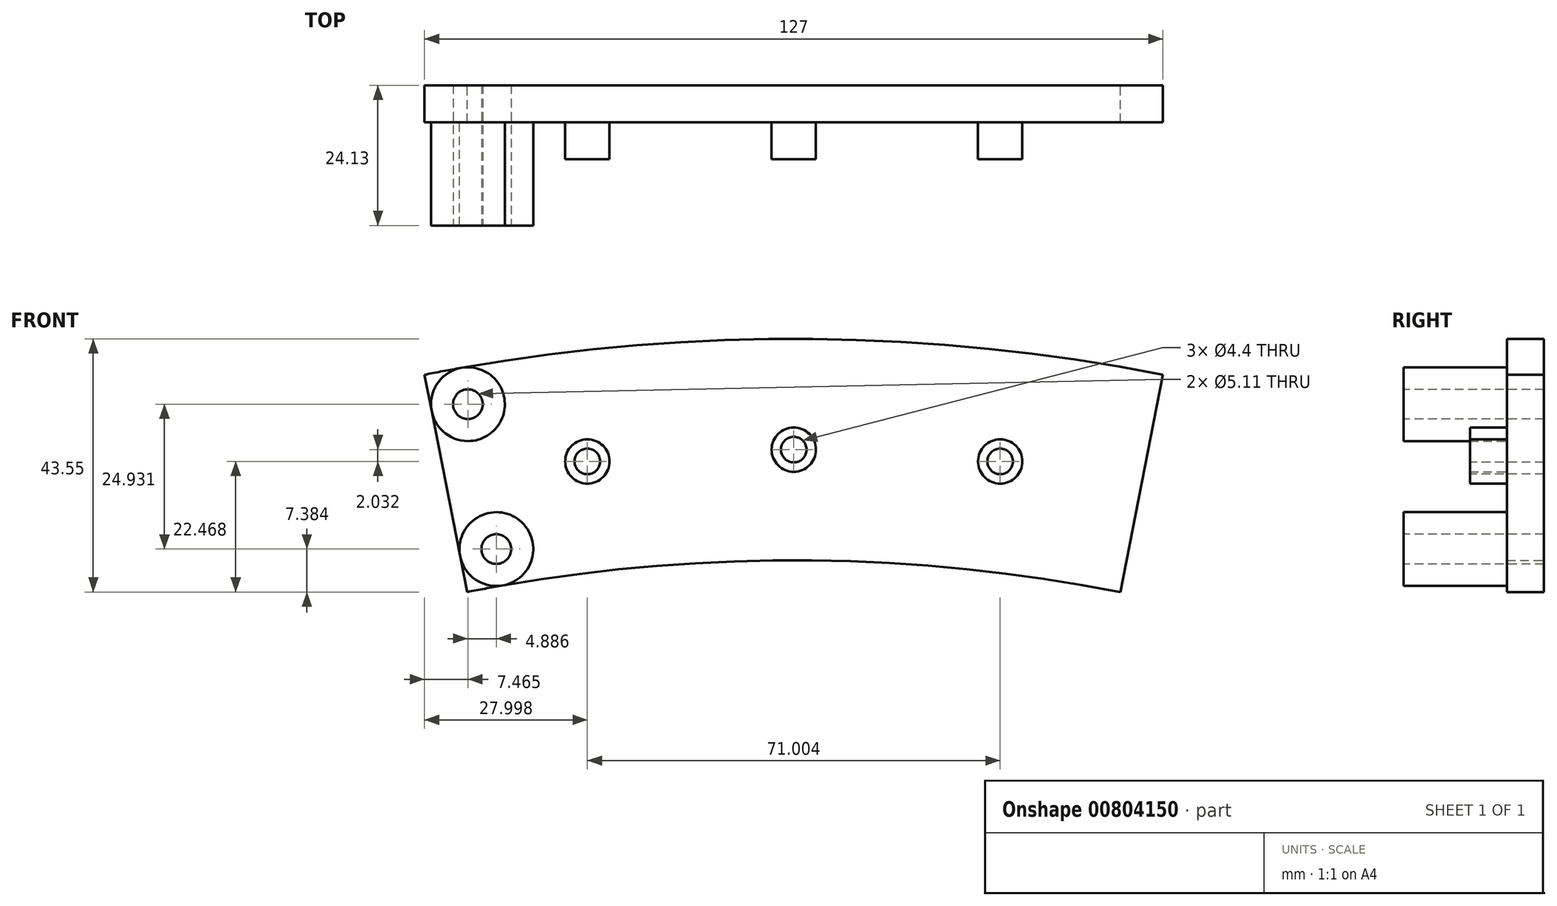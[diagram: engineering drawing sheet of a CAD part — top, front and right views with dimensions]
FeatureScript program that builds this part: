
annotation { "Feature Type Name" : "Feature", "Feature Type Description" : "" }
export const myFeature = defineFeature(function(context is Context, id is Id, definition is map)
    precondition{}
    {
        {
            var Q0;
            Q0=qCreatedBy(makeId("Front.planeOp"),FACE);
            var sketch = newSketch(context, id + "F0", { "sketchPlane" : qUnion([Q0])});
            skArc(sketch, "E0", {"start": v(63.5, 324.04) * mm, "mid": v(0, 330.2) * mm, "end": v(-63.5, 324.04) * mm});
            skLineSegment(sketch, "E1", {"start": v(-56.17, 286.65) * mm, "end": v(-63.5, 324.04) * mm});
            skLineSegment(sketch, "E2", {"start": v(56.17, 286.65) * mm, "end": v(63.5, 324.04) * mm});
            skLineSegment(sketch, "E3", {"start": v(-63.5, 324.04) * mm, "end": v(63.5, 324.04) * mm, "construction": true});
            skArc(sketch, "E4.0", {"start": v(56.17, 286.65) * mm, "mid": v(0, 292.1) * mm, "end": v(-56.17, 286.65) * mm});
            skSolve(sketch);
        }
        {
            var Q0;
            Q0 = qSketchRegion(id + "F0", true);
            extrude(context, id + "F1", {"entities" : qUnion([Q0]), "depth" : 6.35 * mm, "offsetDistance" : 25.4 * mm});
        }
        {
            var Q0;
            Q0=makeQuery(id+"F1.opExtrude","CAP_FACE",FACE,{"disambiguationData":[OSD([sQuery(id+"F0.wireOp",EDGE,"E0"),sQuery(id+"F0.wireOp",EDGE,"E1"),sQuery(id+"F0.wireOp",EDGE,"E2"),sQuery(id+"F0.wireOp",EDGE,"E4.0")])],"isStart":false});
            var sketch = newSketch(context, id + "F2", { "sketchPlane" : qUnion([Q0])});
            skPoint(sketch, "E5.1.end.orphan", {"position": v(-63.5, 324.04) * mm});
            skPoint(sketch, "E5.1.start.orphan", {"position": v(-56.17, 286.65) * mm});
            skLineSegment(sketch, "E6.0", {"start": v(-56.17, 286.65) * mm, "end": v(-63.5, 324.04) * mm, "construction": true});
            skLineSegment(sketch, "E7", {"start": v(-57.26, 325.2) * mm, "end": v(-49.93, 287.8) * mm, "construction": true});
            skArc(sketch, "E8.0", {"start": v(63.5, 324.04) * mm, "mid": v(0, 330.2) * mm, "end": v(-63.5, 324.04) * mm, "construction": true});
            skArc(sketch, "E9.0", {"start": v(56.17, 286.65) * mm, "mid": v(0, 292.1) * mm, "end": v(-56.17, 286.65) * mm, "construction": true});
            skCircle(sketch, "E10", {"center": v(-51.15, 294.03) * mm, "radius": 6.35 * mm});
            skCircle(sketch, "E11", {"center": v(-56.04, 318.97) * mm, "radius": 6.35 * mm});
            skSolve(sketch);
        }
        {
            var Q0;
            Q0 = qSketchRegion(id + "F2", true);
            extrude(context, id + "F3", {"entities" : qUnion([Q0]), "operationType" : NewBodyOperationType.ADD, "depth" : 17.78 * mm, "offsetDistance" : 25.4 * mm});
        }
        {
            var Q0;
            Q0=makeQuery(id+"F3.opExtrude","CAP_FACE",FACE,{"disambiguationData":[OSD([sQuery(id+"F2.wireOp",EDGE,"E11")])],"isStart":false});
            var sketch = newSketch(context, id + "F4", { "sketchPlane" : qUnion([Q0])});
            skCircle(sketch, "E12.0", {"center": v(-56.04, 318.97) * mm, "radius": 6.35 * mm, "construction": true});
            skCircle(sketch, "E12.1", {"center": v(-51.15, 294.03) * mm, "radius": 6.35 * mm, "construction": true});
            skSolve(sketch);
        }
        {
            var Q0;
            Q0=sQuery(id+"F4.wireOp",VERTEX,"E12.0.center");
            var Q1;
            Q1=sQuery(id+"F4.wireOp",VERTEX,"E12.1.center");
            var Q2;
            Q2=makeQuery(id+"F1.opExtrude","SWEPT_BODY",BODY,{"disambiguationData":[OSD([sQuery(id+"F0.wireOp",EDGE,"E0"),sQuery(id+"F0.wireOp",EDGE,"E1"),sQuery(id+"F0.wireOp",EDGE,"E2"),sQuery(id+"F0.wireOp",EDGE,"E4.0")])]});
            hole(context, id + "F5", {"style" : HoleStyle.SIMPLE, "endStyle" : HoleEndStyle.THROUGH, "standardTappedOrClearance" : lookupTablePath({ "fit" : "Normal (ASME)", "standard" : "ANSI", "size" : "#10", "type" : "Clearance" }), "standardBlindInLast" : lookupTablePath({ "fit" : "Free", "standard" : "ANSI", "size" : "#10", "type" : "Clearance" }), "holeDiameter" : 5.1 * mm, "majorDiameter" : 6.35 * mm, "tappedDepth" : 9.52 * mm, "tapClearance" : 3, "startFromSketch" : true, "locations" : qUnion([Q0, Q1]), "scope" : qUnion([Q2])});
        }
        {
            var Q0;
            {var subQ0=sQuery(id+"F0.wireOp",EDGE,"E2");var subQ1=makeQuery(id+"F1.opExtrude","SWEPT_FACE",FACE,{"disambiguationData":[OSD([subQ0])]});var subQ2=sQuery(id+"F2.wireOp",EDGE,"E11");var subQ3=makeQuery(id+"F3.opExtrude","SWEPT_FACE",FACE,{"disambiguationData":[OSD([subQ2])]});var subQ4=sQuery(id+"F0.wireOp",EDGE,"E1");var subQ5=makeQuery(id+"F1.opExtrude","SWEPT_FACE",FACE,{"disambiguationData":[OSD([subQ4])]});var subQ6=sQuery(id+"F0.wireOp",EDGE,"E4.0");var subQ7=sQuery(id+"F0.wireOp",EDGE,"E0");var subQ8=makeQuery(id+"F1.opExtrude","CAP_FACE",FACE,{"disambiguationData":[OSD([subQ7,subQ4,subQ0,subQ6])],"isStart":false});var subQ9=sQuery(id+"F2.wireOp",EDGE,"E10");var subQ10=makeQuery(id+"F1.opExtrude","SWEPT_FACE",FACE,{"disambiguationData":[OSD([subQ7])]});var subQ11=makeQuery(id+"F1.opExtrude","SWEPT_FACE",FACE,{"disambiguationData":[OSD([subQ6])]});var subQ12=makeQuery(id+"F3.opExtrude","SWEPT_FACE",FACE,{"disambiguationData":[OSD([subQ9])]});Q0=makeQuery(id+"FSiQkjA1CRliBXU_1.1.F3.boolean.opBoolean","SPLIT",FACE,{"disambiguationData":[TD([subQ10,subQ8,subQ5,subQ1,subQ11,subQ12,subQ3,makeQuery(id+"FSiQkjA1CRliBXU_1.1.F3.opExtrude","SWEPT_FACE",FACE,{"disambiguationData":[OSD([subQ9])]}),makeQuery(id+"FSiQkjA1CRliBXU_1.1.F3.opExtrude","SWEPT_FACE",FACE,{"disambiguationData":[OSD([subQ2])]})])],"derivedFrom":makeQuery(id+"F3.boolean.opBoolean","SPLIT",FACE,{"disambiguationData":[TD([subQ10,subQ8,subQ5,subQ1,subQ11,subQ12,subQ3])],"derivedFrom":subQ8})});}
            var sketch = newSketch(context, id + "F6", { "sketchPlane" : qUnion([Q0])});
            skLineSegment(sketch, "E13", {"start": v(0, 330.2) * mm, "end": v(0, 292.1) * mm, "construction": true});
            skArc(sketch, "E14.1", {"start": v(50.06, 287.78) * mm, "mid": v(0, 292.1) * mm, "end": v(-50.06, 287.78) * mm, "construction": true});
            skArc(sketch, "E15.0", {"start": v(89.55, 297.99) * mm, "mid": v(0, 311.15) * mm, "end": v(-89.55, 297.99) * mm, "construction": true});
            skPoint(sketch, "E16", {"position": v(0, 311.15) * mm});
            skCircle(sketch, "E17", {"center": v(0, 311.15) * mm, "radius": 3.81 * mm});
            skCircle(sketch, "E18", {"center": v(-35.5, 309.12) * mm, "radius": 3.81 * mm});
            skCircle(sketch, "E19", {"center": v(35.5, 309.12) * mm, "radius": 3.81 * mm});
            skLineSegment(sketch, "E20", {"start": v(-35.5, 309.12) * mm, "end": v(0, 311.15) * mm, "construction": true});
            skLineSegment(sketch, "E21", {"start": v(35.5, 309.12) * mm, "end": v(0, 311.15) * mm, "construction": true});
            skSolve(sketch);
        }
        {
            var Q0;
            Q0 = qSketchRegion(id + "F6", true);
            extrude(context, id + "F7", {"entities" : qUnion([Q0]), "operationType" : NewBodyOperationType.ADD, "depth" : 6.35 * mm, "offsetDistance" : 25.4 * mm});
        }
        {
            var Q0;
            Q0=makeQuery(id+"F7.opExtrude","CAP_FACE",FACE,{"disambiguationData":[OSD([sQuery(id+"F6.wireOp",EDGE,"E18")])],"isStart":false});
            var sketch = newSketch(context, id + "F8", { "sketchPlane" : qUnion([Q0])});
            skPoint(sketch, "E22", {"position": v(-35.5, 309.12) * mm});
            skCircle(sketch, "E23.0", {"center": v(0, 311.15) * mm, "radius": 3.81 * mm, "construction": true});
            skCircle(sketch, "E24.0", {"center": v(35.5, 309.12) * mm, "radius": 3.81 * mm, "construction": true});
            skSolve(sketch);
        }
        {
            var Q0;
            Q0=sQuery(id+"F8.wireOp",VERTEX,"E22");
            var Q1;
            Q1=sQuery(id+"F8.wireOp",VERTEX,"E23.0.center");
            var Q2;
            Q2=sQuery(id+"F8.wireOp",VERTEX,"E24.0.center");
            var Q3;
            Q3=makeQuery(id+"F1.opExtrude","SWEPT_BODY",BODY,{"disambiguationData":[OSD([sQuery(id+"F0.wireOp",EDGE,"E0"),sQuery(id+"F0.wireOp",EDGE,"E1"),sQuery(id+"F0.wireOp",EDGE,"E2"),sQuery(id+"F0.wireOp",EDGE,"E4.0")])]});
            hole(context, id + "F9", {"style" : HoleStyle.SIMPLE, "endStyle" : HoleEndStyle.THROUGH, "standardTappedOrClearance" : lookupTablePath({ "fit" : "Normal", "standard" : "ISO", "size" : "M4", "type" : "Clearance" }), "standardBlindInLast" : lookupTablePath({ "fit" : "Standard", "standard" : "ISO", "size" : "M4", "type" : "Clearance" }), "holeDiameter" : 4.4 * mm, "majorDiameter" : 6.35 * mm, "tappedDepth" : 9.52 * mm, "tapClearance" : 3, "startFromSketch" : true, "locations" : qUnion([Q0, Q1, Q2]), "scope" : qUnion([Q3])});
        }
    });
